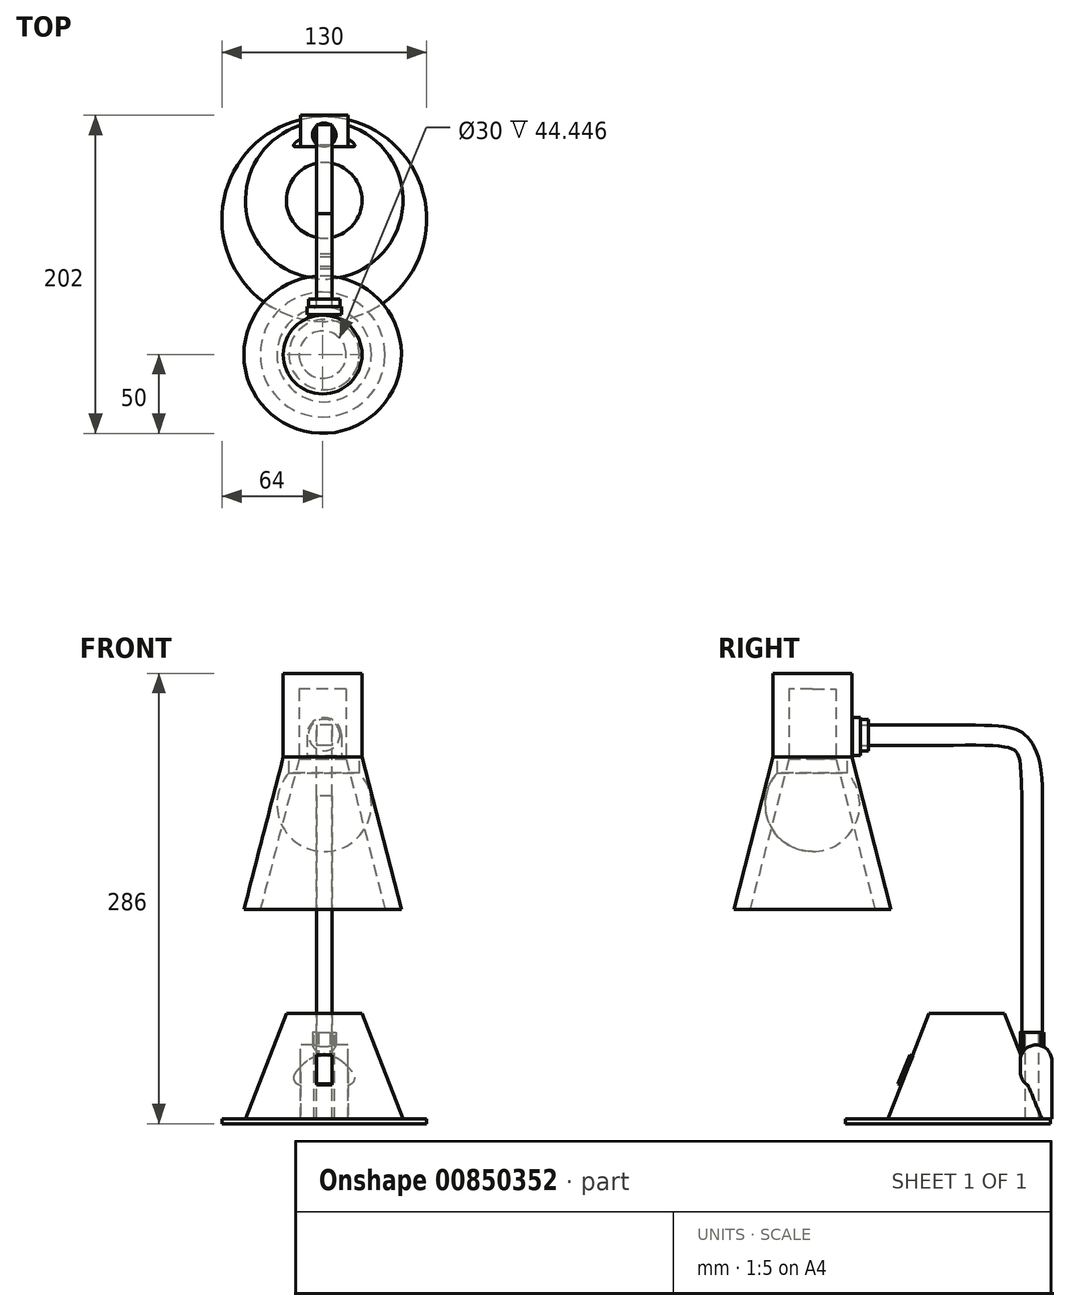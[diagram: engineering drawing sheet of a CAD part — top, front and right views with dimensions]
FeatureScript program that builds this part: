
annotation { "Feature Type Name" : "Feature", "Feature Type Description" : "" }
export const myFeature = defineFeature(function(context is Context, id is Id, definition is map)
    precondition{}
    {
        {
            var Q0;
            Q0=qCreatedBy(makeId("Top.planeOp"),FACE);
            var sketch = newSketch(context, id + "F0", { "sketchPlane" : qUnion([Q0])});
            skPoint(sketch, "E0.middle", {"position": v(0, 0) * mm});
            skCircle(sketch, "E1", {"center": v(0, 0) * mm, "radius": 65 * mm});
            skSolve(sketch);
        }
        {
            var Q0;
            Q0=qSketchRegion(id+"F0",true);
            extrude(context, id + "F1", {"entities" : qUnion([Q0]), "depth" : 3 * mm, "offsetDistance" : 25 * mm});
        }
        {
            var Q0;
            Q0=makeQuery(id+"F1.opExtrude","CAP_FACE",FACE,{"disambiguationData":[OSD([sQuery(id+"F0.wireOp",EDGE,"E1")])],"isStart":false});
            var sketch = newSketch(context, id + "F2", { "sketchPlane" : qUnion([Q0])});
            skCircle(sketch, "E2", {"center": v(0, 12) * mm, "radius": 50 * mm});
            skSolve(sketch);
        }
        {
            var Q0;
            Q0=qCreatedBy(makeId("Top.planeOp"),FACE);
            cPlane(context, id + "F3", {"entities" : qUnion([Q0]), "cplaneType" : CPlaneType.OFFSET, "offset" : 70 * mm, "width" : 150 * mm, "height" : 150 * mm});
        }
        {
            var Q0;
            Q0=qCreatedBy(id+"F3.planeOp",FACE);
            var sketch = newSketch(context, id + "F4", { "sketchPlane" : qUnion([Q0])});
            skCircle(sketch, "E3", {"center": v(0, 12) * mm, "radius": 24 * mm});
            skSolve(sketch);
        }
        {
            var Q1;
            Q1=makeQuery(id+"F2.imprint","IMPRINT",FACE,{"disambiguationData":[TD([[makeQuery(id+"F2.imprint","IMPRINT",EDGE,{"derivedFrom":sQuery(id+"F2.wireOp",EDGE,"E2")}),1.0]])]});
            var Q2;
            Q2=makeQuery(id+"F4.imprint","IMPRINT",FACE,{"disambiguationData":[TD([[makeQuery(id+"F4.imprint","IMPRINT",EDGE,{"derivedFrom":sQuery(id+"F4.wireOp",EDGE,"E3")}),1.0]])]});
            loft(context, id + "F5", {"operationType" : NewBodyOperationType.ADD, "sheetProfilesArray" : [{ "sheetProfileEntities" : qUnion([Q1]) }, { "sheetProfileEntities" : qUnion([Q2]) }]});
        }
        {
            var Q0;
            Q0=qCreatedBy(makeId("Right.planeOp"),FACE);
            var sketch = newSketch(context, id + "F6", { "sketchPlane" : qUnion([Q0])});
            skLineSegment(sketch, "E4.bottom", {"start": v(46, 40) * mm, "end": v(56, 40) * mm});
            skLineSegment(sketch, "E4.top", {"start": v(46, 23) * mm, "end": v(56, 23) * mm});
            skLineSegment(sketch, "E4.left", {"start": v(46, 40) * mm, "end": v(46, 23) * mm});
            skLineSegment(sketch, "E4.right", {"start": v(56, 40) * mm, "end": v(56, 23) * mm});
            skSolve(sketch);
        }
        {
            var Q0;
            Q0=makeQuery(id+"F6.imprint","IMPRINT",FACE,{"disambiguationData":[TD([[makeQuery(id+"F6.imprint","IMPRINT",EDGE,{"derivedFrom":sQuery(id+"F6.wireOp",EDGE,"E4.bottom")}),-1.0]])]});
            extrude(context, id + "F7", {"entities" : qUnion([Q0]), "operationType" : NewBodyOperationType.REMOVE, "endBound" : BoundingType.SYMMETRIC, "depth" : 60 * mm, "offsetDistance" : 25 * mm});
        }
        {
            var Q0;
            Q0=makeQuery(id+"F7.boolean.opBoolean","COPY",EDGE,{"derivedFrom":makeQuery(id+"F7.opExtrude","SWEPT_EDGE",EDGE,{"disambiguationData":[OSD([sQuery(id+"F6.wireOp",EDGE,"E4.top"),sQuery(id+"F6.wireOp",EDGE,"E4.left")])]})});
            fillet(context, id + "F8", {"entities" : qUnion([Q0]), "radius" : 10 * mm, "tangentPropagation" : true, "allowEdgeOverflow" : false});
        }
        {
            var Q0;
            Q0=qCreatedBy(makeId("Right.planeOp"),FACE);
            var sketch = newSketch(context, id + "F9", { "sketchPlane" : qUnion([Q0])});
            skLineSegment(sketch, "E5", {"start": v(46, 3) * mm, "end": v(46, 40) * mm});
            skLineSegment(sketch, "E6", {"start": v(66, 3) * mm, "end": v(66, 40) * mm});
            skArc(sketch, "E7", {"start": v(56, 50) * mm, "mid": v(63.07, 47.07) * mm, "end": v(66, 40) * mm});
            skArc(sketch, "E8", {"start": v(46, 40) * mm, "mid": v(48.93, 47.07) * mm, "end": v(56, 50) * mm});
            skPoint(sketch, "E9", {"position": v(46, 53) * mm});
            skPoint(sketch, "E10", {"position": v(66, 53) * mm});
            skLineSegment(sketch, "E11", {"start": v(46, 3) * mm, "end": v(66, 3) * mm});
            skSolve(sketch);
        }
        {
            var Q0;
            Q0=qSketchRegion(id+"F9",true);
            extrude(context, id + "F10", {"entities" : qUnion([Q0]), "operationType" : NewBodyOperationType.ADD, "endBound" : BoundingType.SYMMETRIC, "depth" : 30 * mm, "offsetDistance" : 25 * mm});
        }
        {
            var Q0;
            Q0=makeQuery(id+"F1.opExtrude","CAP_FACE",FACE,{"disambiguationData":[OSD([sQuery(id+"F0.wireOp",EDGE,"E1")])],"isStart":false});
            var sketch = newSketch(context, id + "F11", { "sketchPlane" : qUnion([Q0])});
            skCircle(sketch, "E12", {"center": v(0, 53.5) * mm, "radius": 7.5 * mm});
            skSolve(sketch);
        }
        {
            var Q0;
            Q0=qSketchRegion(id+"F11",true);
            extrude(context, id + "F12", {"entities" : qUnion([Q0]), "operationType" : NewBodyOperationType.ADD, "depth" : 55 * mm, "offsetDistance" : 25 * mm});
        }
        {
            var Q0;
            Q0=makeQuery(id+"F12.opExtrude","CAP_FACE",FACE,{"disambiguationData":[OSD([sQuery(id+"F11.wireOp",EDGE,"E12")])],"isStart":false});
            var sketch = newSketch(context, id + "F13", { "sketchPlane" : qUnion([Q0])});
            skCircle(sketch, "E13.0", {"center": v(0, 53.5) * mm, "radius": 6.5 * mm});
            skSolve(sketch);
        }
        {
            var Q0;
            Q0=qSketchRegion(id+"F13",true);
            var Q1;
            Q1=makeQuery(id+"F1.opExtrude","CAP_FACE",FACE,{"disambiguationData":[OSD([sQuery(id+"F0.wireOp",EDGE,"E1")])],"isStart":false});
            extrude(context, id + "F14", {"entities" : qUnion([Q0]), "operationType" : NewBodyOperationType.REMOVE, "endBound" : BoundingType.UP_TO_SURFACE, "oppositeDirection" : true, "depth" : 25 * mm, "endBoundEntityFace" : qUnion([Q1]), "offsetDistance" : 25 * mm});
        }
        {
            var Q0;
            Q0=makeQuery(id+"F5.opLoft","CAP_FACE",FACE,{"disambiguationData":[OSD([makeQuery(id+"F4.imprint","IMPRINT",FACE,{"disambiguationData":[TD([[makeQuery(id+"F4.imprint","IMPRINT",EDGE,{"derivedFrom":sQuery(id+"F4.wireOp",EDGE,"E3")}),1.0]])]})])],"isStart":true});
            cPlane(context, id + "F15", {"entities" : qUnion([Q0]), "cplaneType" : CPlaneType.OFFSET, "offset" : 5 * mm, "oppositeDirection" : true, "width" : 150 * mm, "height" : 150 * mm});
        }
        {
            var Q0;
            Q0=qCreatedBy(makeId("Right.planeOp"),FACE);
            cPlane(context, id + "F16", {"entities" : qUnion([Q0]), "cplaneType" : CPlaneType.OFFSET, "offset" : 5 * mm, "oppositeDirection" : true, "width" : 150 * mm, "height" : 150 * mm});
        }
        {
            var Q0;
            Q0=qCreatedBy(id+"F16.planeOp",FACE);
            var sketch = newSketch(context, id + "F17", { "sketchPlane" : qUnion([Q0])});
            skLineSegment(sketch, "E14.0", {"start": v(46, 58) * mm, "end": v(61, 58) * mm});
            skLineSegment(sketch, "E15.0", {"start": v(47, 58) * mm, "end": v(60, 58) * mm});
            skSolve(sketch);
        }
        {
            var Q0;
            Q0=qCreatedBy(id+"F16.planeOp",FACE);
            var sketch = newSketch(context, id + "F18", { "sketchPlane" : qUnion([Q0])});
            skLineSegment(sketch, "E16.bottom", {"start": v(60, 3) * mm, "end": v(47, 3) * mm});
            skLineSegment(sketch, "E17", {"start": v(47, 58) * mm, "end": v(47, 208) * mm});
            skLineSegment(sketch, "E18", {"start": v(60, 58) * mm, "end": v(60, 208) * mm});
            skFitSpline(sketch, "E19", {"points": [v(60, 208) * mm, v(48.55, 247.3) * mm, v(3.39, 253.37) * mm], "startDerivative": vector(2.49, 149.87) * mm, "endDerivative": vector(-184.82, 1.92) * mm});
            skFitSpline(sketch, "E20", {"points": [v(47, 208) * mm, v(45.35, 231.77) * mm, v(3.39, 240.37) * mm], "startDerivative": vector(-2.36, 61.21) * mm, "endDerivative": vector(-191.9, -1.87) * mm});
            skLineSegment(sketch, "E21", {"start": v(3.39, 253.37) * mm, "end": v(-50.61, 253.37) * mm});
            skLineSegment(sketch, "E22", {"start": v(3.39, 240.37) * mm, "end": v(-50.61, 240.37) * mm});
            skLineSegment(sketch, "E23", {"start": v(-50.61, 253.37) * mm, "end": v(-50.61, 240.37) * mm});
            skLineSegment(sketch, "E24", {"start": v(60, 58) * mm, "end": v(60, 3) * mm});
            skLineSegment(sketch, "E25", {"start": v(47, 58) * mm, "end": v(47, 3) * mm});
            skSolve(sketch);
        }
        {
            var Q0;
            Q0=makeQuery(id+"F18.imprint","IMPRINT",FACE,{"disambiguationData":[TD([[makeQuery(id+"F18.imprint","IMPRINT",EDGE,{"derivedFrom":sQuery(id+"F18.wireOp",EDGE,"E16.bottom")}),-1.0]])]});
            extrude(context, id + "F19", {"entities" : qUnion([Q0]), "operationType" : NewBodyOperationType.ADD, "depth" : 10 * mm, "offsetDistance" : 25 * mm});
        }
        {
            var Q0;
            Q0=makeQuery(id+"F19.opExtrude","SWEPT_FACE",FACE,{"disambiguationData":[OSD([sQuery(id+"F18.wireOp",EDGE,"E23")])]});
            var sketch = newSketch(context, id + "F20", { "sketchPlane" : qUnion([Q0])});
            skCircle(sketch, "E26", {"center": v(0, 246.87) * mm, "radius": 10 * mm});
            skPoint(sketch, "E26.centerSnap0", {"position": v(5, 246.87) * mm});
            skSolve(sketch);
        }
        {
            var Q0;
            Q0=makeQuery(id+"F20.imprint","IMPRINT",FACE,{"disambiguationData":[TD([[makeQuery(id+"F20.imprint","IMPRINT",EDGE,{"derivedFrom":sQuery(id+"F20.wireOp",EDGE,"E26")}),1.0]])]});
            extrude(context, id + "F21", {"entities" : qUnion([Q0]), "operationType" : NewBodyOperationType.ADD, "depth" : 5 * mm, "offsetDistance" : 25 * mm});
        }
        {
            var Q0;
            Q0=makeQuery(id+"F21.opExtrude","CAP_FACE",FACE,{"disambiguationData":[OSD([sQuery(id+"F18.wireOp",EDGE,"E21"),sQuery(id+"F18.wireOp",EDGE,"E22"),sQuery(id+"F18.wireOp",EDGE,"E23"),sQuery(id+"F20.wireOp",EDGE,"E26")])],"isStart":false});
            var sketch = newSketch(context, id + "F22", { "sketchPlane" : qUnion([Q0])});
            skArc(sketch, "E27", {"start": v(0, 257.87) * mm, "mid": v(7.78, 254.65) * mm, "end": v(11, 246.87) * mm});
            skArc(sketch, "E28", {"start": v(0, 257.87) * mm, "mid": v(-7.78, 254.65) * mm, "end": v(-11, 246.87) * mm});
            skLineSegment(sketch, "E29.bottom", {"start": v(-11, 246.87) * mm, "end": v(11, 246.87) * mm});
            skLineSegment(sketch, "E29.top", {"start": v(-11, 234) * mm, "end": v(11, 234) * mm});
            skLineSegment(sketch, "E29.left", {"start": v(-11, 246.87) * mm, "end": v(-11, 234) * mm});
            skLineSegment(sketch, "E29.right", {"start": v(11, 246.87) * mm, "end": v(11, 234) * mm});
            skSolve(sketch);
        }
        {
            var Q0;
            Q0=qSketchRegion(id+"F22",true);
            extrude(context, id + "F23", {"entities" : qUnion([Q0]), "operationType" : NewBodyOperationType.ADD, "depth" : 5 * mm, "offsetDistance" : 25 * mm});
        }
        {
            var Q0;
            Q0=qCreatedBy(makeId("Right.planeOp"),FACE);
            var sketch = newSketch(context, id + "F24", { "sketchPlane" : qUnion([Q0])});
            skLineSegment(sketch, "E30", {"start": v(0, 0) * mm, "end": v(0, 150) * mm});
            skLineSegment(sketch, "E31", {"start": v(0, 0) * mm, "end": v(-50, 0) * mm});
            skLineSegment(sketch, "E32", {"start": v(-50, 0) * mm, "end": v(-25, 96.82) * mm});
            skLineSegment(sketch, "E33", {"start": v(-25, 96.82) * mm, "end": v(-25, 150) * mm});
            skLineSegment(sketch, "E34", {"start": v(-25, 150) * mm, "end": v(0, 150) * mm});
            skSolve(sketch);
        }
        {
            var Q0;
            Q0=makeQuery(id+"F24.imprint","IMPRINT",FACE,{"disambiguationData":[TD([[makeQuery(id+"F24.imprint","IMPRINT",EDGE,{"derivedFrom":sQuery(id+"F24.wireOp",EDGE,"E30")}),1.0]])]});
            var Q1;
            Q1=sQuery(id+"F24.wireOp",EDGE,"E30");
            revolve(context, id + "F25", {"surfaceOperationType" : NewSurfaceOperationType.NEW, "entities" : qUnion([Q0]), "axis" : qUnion([Q1]), "revolveType" : RevolveType.FULL});
        }
        {
            var Q0;
            Q0=makeQuery(id+"F25.opRevolve","SWEPT_FACE",FACE,{"disambiguationData":[OSD([sQuery(id+"F24.wireOp",EDGE,"E31")])]});
            shell(context, id + "F26", {"entities" : qUnion([Q0]), "thickness" : 10 * mm});
        }
        {
            var Q0;
            Q0=makeQuery(id+"F25.opRevolve","SWEPT_BODY",BODY,{"disambiguationData":[OSD([sQuery(id+"F24.wireOp",EDGE,"E30"),sQuery(id+"F24.wireOp",EDGE,"E31"),sQuery(id+"F24.wireOp",EDGE,"E32"),sQuery(id+"F24.wireOp",EDGE,"E33"),sQuery(id+"F24.wireOp",EDGE,"E34")])]});
            transform(context, id + "F27", {"entities" : qUnion([Q0]), "transformType" : TransformType.TRANSLATION_3D, "dx" : -1 * mm, "dy" : -86 * mm, "dz" : 136 * mm, "makeCopy" : false});
        }
        {
            var Q0;
            Q0=makeQuery(id+"F25.opRevolve","SWEPT_FACE",FACE,{"disambiguationData":[OSD([sQuery(id+"F24.wireOp",EDGE,"E34")])]});
            var sketch = newSketch(context, id + "F28", { "sketchPlane" : qUnion([Q0])});
            skLineSegment(sketch, "E35", {"start": v(0, -61.02) * mm, "end": v(0, -110.98) * mm, "construction": true});
            skPoint(sketch, "E36", {"position": v(0, -86) * mm});
            skSolve(sketch);
        }
        {
            var Q0;
            Q0=qCreatedBy(makeId("Right.planeOp"),FACE);
            var sketch = newSketch(context, id + "F29", { "sketchPlane" : qUnion([Q0])});
            skLineSegment(sketch, "E37", {"start": v(-86, 232.82) * mm, "end": v(-86, 172.82) * mm});
            skLineSegment(sketch, "E38", {"start": v(-86, 232.82) * mm, "end": v(-63.64, 232.82) * mm});
            skLineSegment(sketch, "E39", {"start": v(-63.64, 232.82) * mm, "end": v(-63.64, 222.82) * mm});
            skArc(sketch, "E40", {"start": v(-86, 172.82) * mm, "mid": v(-58.61, 190.58) * mm, "end": v(-63.64, 222.82) * mm});
            skSolve(sketch);
        }
        {
            var Q0;
            Q0=qSketchRegion(id+"F29",true);
            var Q1;
            Q1=sQuery(id+"F29.wireOp",EDGE,"E37");
            revolve(context, id + "F30", {"surfaceOperationType" : NewSurfaceOperationType.NEW, "entities" : qUnion([Q0]), "axis" : qUnion([Q1]), "revolveType" : RevolveType.FULL});
        }
        {
            var Q0;
            Q0=qCreatedBy(makeId("Front.planeOp"),FACE);
            cPlane(context, id + "F31", {"entities" : qUnion([Q0]), "cplaneType" : CPlaneType.OFFSET, "offset" : 25 * mm, "width" : 150 * mm, "height" : 150 * mm});
        }
        {
            var Q0;
            Q0=qCreatedBy(id+"F31.planeOp",FACE);
            var sketch = newSketch(context, id + "F32", { "sketchPlane" : qUnion([Q0])});
            skLineSegment(sketch, "E41.bottom", {"start": v(5, 23) * mm, "end": v(-5, 23) * mm});
            skLineSegment(sketch, "E41.top", {"start": v(5, 43) * mm, "end": v(-5, 43) * mm});
            skLineSegment(sketch, "E41.left", {"start": v(5, 23) * mm, "end": v(5, 43) * mm});
            skLineSegment(sketch, "E41.right", {"start": v(-5, 23) * mm, "end": v(-5, 43) * mm});
            skPoint(sketch, "E41.middle", {"position": v(0, 33) * mm});
            skSolve(sketch);
        }
        {
            var Q0;
            Q0=makeQuery(id+"F32.imprint","IMPRINT",FACE,{"disambiguationData":[TD([[makeQuery(id+"F32.imprint","IMPRINT",EDGE,{"derivedFrom":sQuery(id+"F32.wireOp",EDGE,"E41.bottom")}),-1.0]])]});
            extrude(context, id + "F33", {"entities" : qUnion([Q0]), "depth" : 2 * mm, "offsetDistance" : 25 * mm});
        }
        {
            var Q0;
            Q0=makeQuery(id+"F33.opExtrude","SWEPT_BODY",BODY,{"disambiguationData":[OSD([sQuery(id+"F32.wireOp",EDGE,"E41.bottom"),sQuery(id+"F32.wireOp",EDGE,"E41.top"),sQuery(id+"F32.wireOp",EDGE,"E41.left"),sQuery(id+"F32.wireOp",EDGE,"E41.right")])]});
            var Q1;
            Q1=makeQuery(id+"F33.opExtrude","CAP_EDGE",EDGE,{"disambiguationData":[OSD([sQuery(id+"F32.wireOp",EDGE,"E41.top")])],"isStart":true});
            transform(context, id + "F34", {"entities" : qUnion([Q0]), "transformType" : TransformType.ROTATION, "transformAxis" : qUnion([Q1]), "angle" : 22.82 * degree, "makeCopy" : false});
        }
        {
            var Q0;
            Q0=makeQuery(id+"F33.opExtrude","SWEPT_BODY",BODY,{"disambiguationData":[OSD([sQuery(id+"F32.wireOp",EDGE,"E41.bottom"),sQuery(id+"F32.wireOp",EDGE,"E41.top"),sQuery(id+"F32.wireOp",EDGE,"E41.left"),sQuery(id+"F32.wireOp",EDGE,"E41.right")])]});
            transform(context, id + "F35", {"entities" : qUnion([Q0]), "transformType" : TransformType.TRANSLATION_3D, "dx" : 0 * mm, "dy" : 2.8 * mm, "dz" : 0 * mm, "makeCopy" : false});
        }
    });
